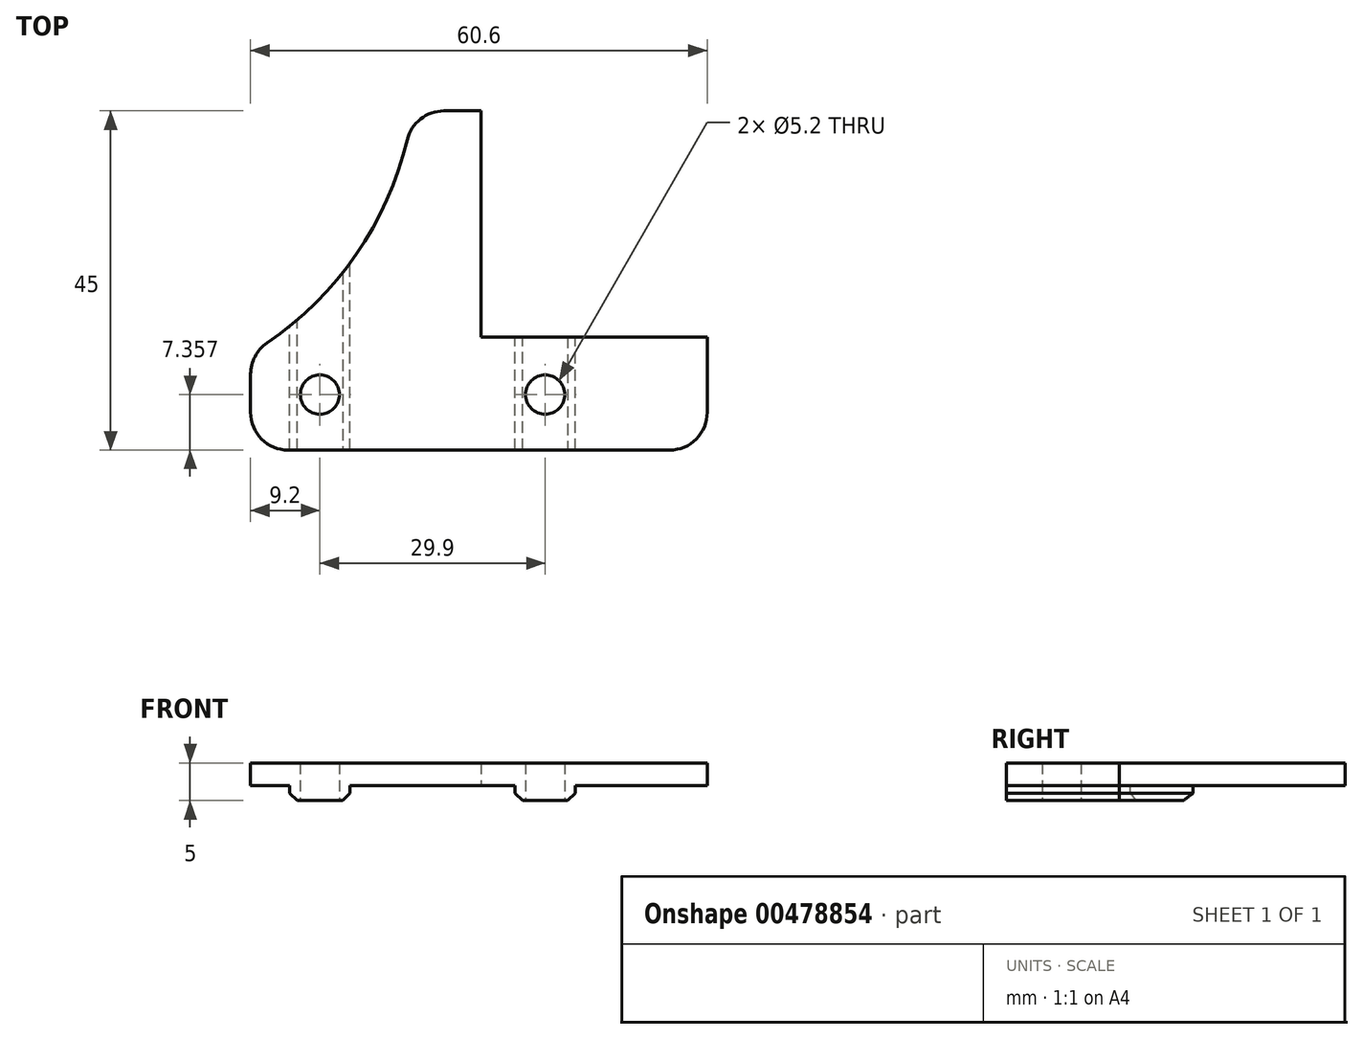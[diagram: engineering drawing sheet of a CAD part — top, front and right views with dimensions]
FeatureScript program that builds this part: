
annotation { "Feature Type Name" : "Feature", "Feature Type Description" : "" }
export const myFeature = defineFeature(function(context is Context, id is Id, definition is map)
    precondition{}
    {
        {
            var Q0;
            Q0=qCreatedBy(makeId("Top.planeOp"),FACE);
            var sketch = newSketch(context, id + "F0", { "sketchPlane" : qUnion([Q0])});
            skLineSegment(sketch, "E0", {"start": v(0, 0) * mm, "end": v(30, 0) * mm});
            skLineSegment(sketch, "E1", {"start": v(30, 0) * mm, "end": v(30, -15) * mm});
            skLineSegment(sketch, "E2", {"start": v(30, -15) * mm, "end": v(-30.6, -15) * mm});
            skLineSegment(sketch, "E3", {"start": v(-30.6, -15) * mm, "end": v(-30.6, -2.18) * mm});
            skLineSegment(sketch, "E4", {"start": v(-9.07, 30) * mm, "end": v(0, 30) * mm});
            skLineSegment(sketch, "E5", {"start": v(0, 30) * mm, "end": v(0, 0) * mm});
            skLineSegment(sketch, "E6", {"start": v(4.3, -15) * mm, "end": v(4.3, 29.92) * mm, "construction": true});
            skLineSegment(sketch, "E7", {"start": v(-17.2, -15) * mm, "end": v(-17.2, 30.52) * mm, "construction": true});
            skLineSegment(sketch, "E8", {"start": v(-25.6, -15) * mm, "end": v(-25.6, 27.4) * mm, "construction": true});
            skLineSegment(sketch, "E9", {"start": v(12.7, -15) * mm, "end": v(12.7, 26.92) * mm, "construction": true});
            skCircle(sketch, "E10", {"center": v(-21.4, -7.64) * mm, "radius": 2.6 * mm});
            skCircle(sketch, "E11", {"center": v(8.5, -7.64) * mm, "radius": 2.6 * mm});
            skArc(sketch, "E12", {"start": v(-30.6, -2.18) * mm, "mid": v(-16.22, 11.5) * mm, "end": v(-9.07, 30) * mm});
            skSolve(sketch);
        }
        {
            var Q0;
            Q0 = qSketchRegion(id + "F0", true);
            extrude(context, id + "F1", {"entities" : qUnion([Q0]), "depth" : 3 * mm});
        }
        {
            var Q0;
            Q0=makeQuery(id+"F1.opExtrude","SWEPT_EDGE",EDGE,{"disambiguationData":[OSD([sQuery(id+"F0.wireOp",EDGE,"E2"),sQuery(id+"F0.wireOp",EDGE,"E3")])]});
            var Q1;
            Q1=makeQuery(id+"F1.opExtrude","SWEPT_EDGE",EDGE,{"disambiguationData":[OSD([sQuery(id+"F0.wireOp",EDGE,"E3"),sQuery(id+"F0.wireOp",EDGE,"E12")])]});
            var Q2;
            Q2=makeQuery(id+"F1.opExtrude","SWEPT_EDGE",EDGE,{"disambiguationData":[OSD([sQuery(id+"F0.wireOp",EDGE,"E2"),sQuery(id+"F0.wireOp",EDGE,"E3")])]});
            var Q3;
            Q3=makeQuery(id+"F1.opExtrude","SWEPT_EDGE",EDGE,{"disambiguationData":[OSD([sQuery(id+"F0.wireOp",EDGE,"E1"),sQuery(id+"F0.wireOp",EDGE,"E2")])]});
            var Q4;
            Q4=makeQuery(id+"F1.opExtrude","SWEPT_EDGE",EDGE,{"disambiguationData":[OSD([sQuery(id+"F0.wireOp",EDGE,"E4"),sQuery(id+"F0.wireOp",EDGE,"E12")])]});
            fillet(context, id + "F2", {"entities" : qUnion([Q0, Q1, Q2, Q3, Q4]), "radius" : 5 * mm, "tangentPropagation" : true, "allowEdgeOverflow" : false});
        }
        {
            var Q0;
            Q0=makeQuery(id+"F0.imprint","IMPRINT",FACE,{"disambiguationData":[TD([[makeQuery(id+"F0.imprint","IMPRINT",EDGE,{"derivedFrom":sQuery(id+"F0.wireOp",EDGE,"E0")}),-1.0]])]});
            var sketch = newSketch(context, id + "F3", { "sketchPlane" : qUnion([Q0])});
            skLineSegment(sketch, "E13", {"start": v(-25.4, -15) * mm, "end": v(-25.4, 1.45) * mm});
            skLineSegment(sketch, "E14", {"start": v(-25.4, -15) * mm, "end": v(-17.4, -15) * mm});
            skLineSegment(sketch, "E15", {"start": v(-17.4, -15) * mm, "end": v(-17.4, 9.81) * mm});
            skLineSegment(sketch, "E16.1.0.0", {"start": v(4.5, 30) * mm, "end": v(12.5, 30) * mm});
            skLineSegment(sketch, "E16.1.0.1", {"start": v(12.5, -15) * mm, "end": v(12.5, 30) * mm});
            skLineSegment(sketch, "E16.1.0.2", {"start": v(4.5, -15) * mm, "end": v(12.5, -15) * mm});
            skLineSegment(sketch, "E16.1.0.3", {"start": v(4.5, -15) * mm, "end": v(4.5, 30) * mm});
            skLineSegment(sketch, "E16.direction1", {"start": v(-25.4, -15) * mm, "end": v(4.5, -15) * mm, "construction": true});
            skLineSegment(sketch, "E17.0", {"start": v(4.5, 0) * mm, "end": v(12.5, 0) * mm});
            skPoint(sketch, "E18.orphan", {"position": v(0, 0) * mm});
            skPoint(sketch, "E19.orphan", {"position": v(30, 0) * mm});
            skArc(sketch, "E20.0", {"start": v(-25.4, 1.45) * mm, "mid": v(-21.13, 5.37) * mm, "end": v(-17.4, 9.81) * mm});
            skPoint(sketch, "E21.orphan", {"position": v(-9.8, 26.16) * mm});
            skPoint(sketch, "E22.orphan", {"position": v(-28.41, -0.79) * mm});
            skSolve(sketch);
        }
        {
            var Q0;
            Q0=makeQuery(id+"F3.imprint","IMPRINT",FACE,{"disambiguationData":[TD([[makeQuery(id+"F3.imprint","IMPRINT",EDGE,{"derivedFrom":sQuery(id+"F3.wireOp",EDGE,"E13")}),-1.0]])]});
            var Q1;
            {var subQ1=sQuery(id+"F3.wireOp",EDGE,"E16.1.0.2");Q1=makeQuery(id+"F3.imprint","IMPRINT",FACE,{"disambiguationData":[TD([[makeQuery(id+"F3.imprint","IMPRINT",EDGE,{"derivedFrom":subQ1}),-1.0]])]});}
            extrude(context, id + "F4", {"entities" : qUnion([Q0, Q1]), "operationType" : NewBodyOperationType.ADD, "oppositeDirection" : true, "depth" : 2 * mm});
        }
        {
            var Q0;
            Q0=makeQuery(id+"F4.opExtrude","CAP_EDGE",EDGE,{"disambiguationData":[OSD([sQuery(id+"F3.wireOp",EDGE,"E13")])],"isStart":false});
            var Q1;
            Q1=makeQuery(id+"F4.opExtrude","CAP_EDGE",EDGE,{"disambiguationData":[OSD([sQuery(id+"F3.wireOp",EDGE,"E15")])],"isStart":false});
            var Q2;
            Q2=makeQuery(id+"F4.opExtrude","CAP_EDGE",EDGE,{"disambiguationData":[OSD([sQuery(id+"F3.wireOp",EDGE,"E16.1.0.3")])],"isStart":false});
            var Q3;
            Q3=makeQuery(id+"F4.opExtrude","CAP_EDGE",EDGE,{"disambiguationData":[OSD([sQuery(id+"F3.wireOp",EDGE,"E16.1.0.1")])],"isStart":false});
            chamfer(context, id + "F5", {"entities" : qUnion([Q0, Q1, Q2, Q3]), "width" : 1 * mm, "tangentPropagation" : true});
        }
    });
